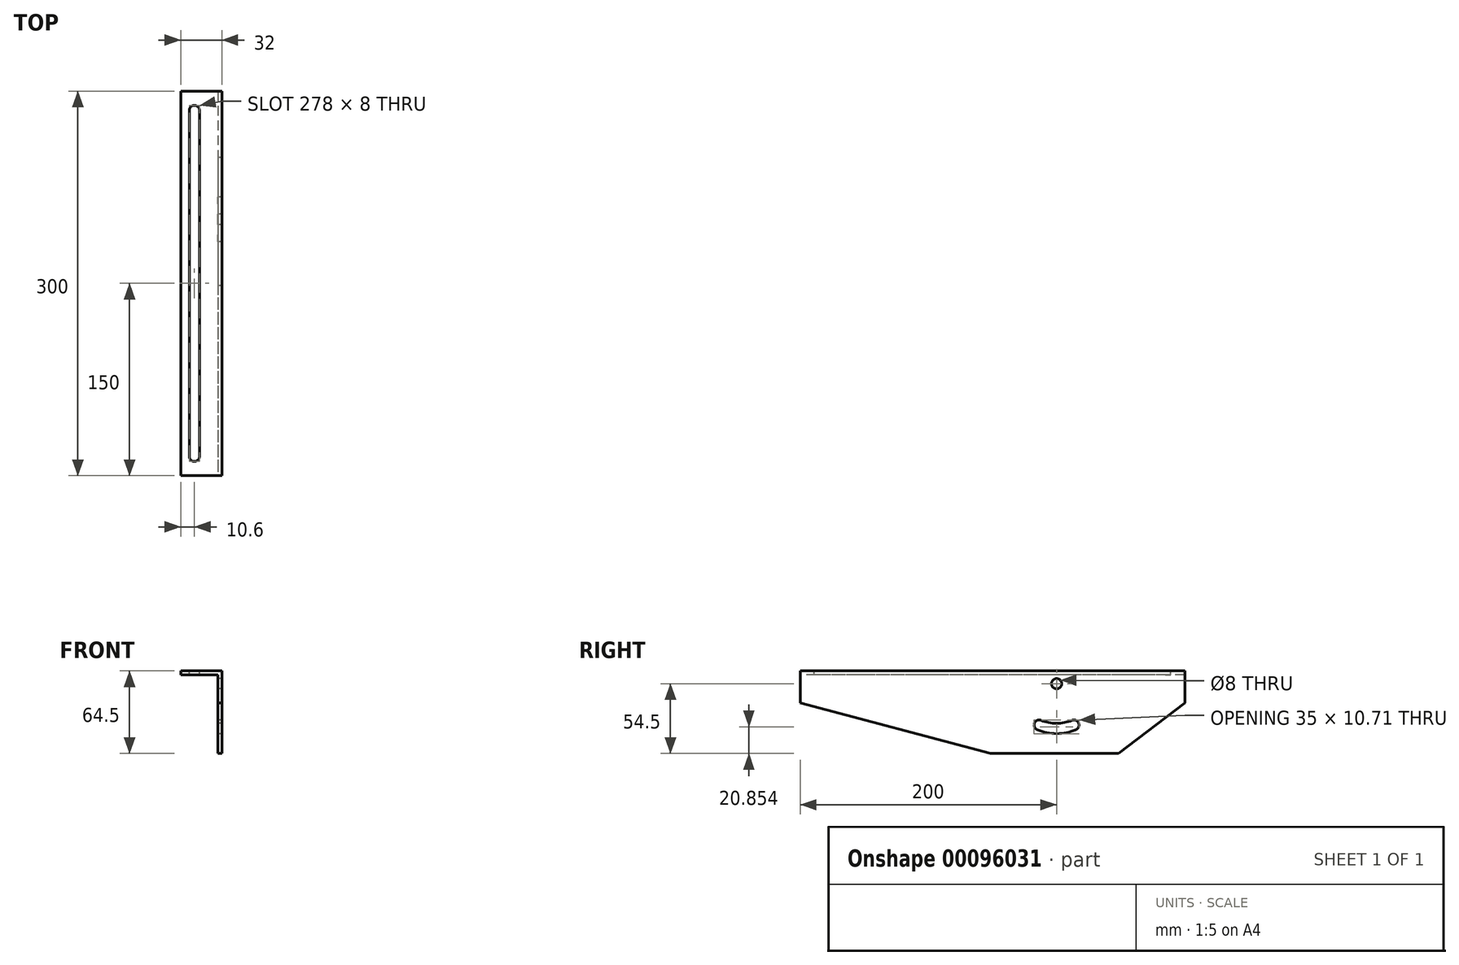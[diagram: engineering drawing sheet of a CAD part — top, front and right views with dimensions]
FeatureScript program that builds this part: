
annotation { "Feature Type Name" : "Feature", "Feature Type Description" : "" }
export const myFeature = defineFeature(function(context is Context, id is Id, definition is map)
    precondition{}
    {
        {
            var Q0;
            Q0=qCreatedBy(makeId("Right.planeOp"),FACE);
            var sketch = newSketch(context, id + "F0", { "sketchPlane" : qUnion([Q0])});
            skLineSegment(sketch, "E0", {"start": v(150, 0) * mm, "end": v(-150, 0) * mm});
            skLineSegment(sketch, "E1", {"start": v(-150, 0) * mm, "end": v(-150, -25) * mm});
            skLineSegment(sketch, "E2", {"start": v(150, 0) * mm, "end": v(150, -25) * mm});
            skLineSegment(sketch, "E3", {"start": v(150, -25) * mm, "end": v(98.38, -64.5) * mm});
            skLineSegment(sketch, "E4", {"start": v(98.38, -64.5) * mm, "end": v(-1.62, -64.5) * mm});
            skLineSegment(sketch, "E5", {"start": v(-1.62, -64.5) * mm, "end": v(-150, -25) * mm});
            skSolve(sketch);
        }
        {
            var Q0;
            Q0=makeQuery(id+"F0.imprint","IMPRINT",FACE,{"disambiguationData":[TD([[makeQuery(id+"F0.imprint","IMPRINT",EDGE,{"derivedFrom":sQuery(id+"F0.wireOp",EDGE,"E0")}),1.0]])]});
            extrude(context, id + "F1", {"entities" : qUnion([Q0]), "depth" : 3 * mm});
        }
        {
            var Q0;
            Q0=makeQuery(id+"F1.opExtrude","CAP_FACE",FACE,{"disambiguationData":[OSD([sQuery(id+"F0.wireOp",EDGE,"E0"),sQuery(id+"F0.wireOp",EDGE,"E1"),sQuery(id+"F0.wireOp",EDGE,"E2"),sQuery(id+"F0.wireOp",EDGE,"E3"),sQuery(id+"F0.wireOp",EDGE,"E4"),sQuery(id+"F0.wireOp",EDGE,"E5")])],"isStart":true});
            var sketch = newSketch(context, id + "F2", { "sketchPlane" : qUnion([Q0])});
            skLineSegment(sketch, "E6.bottom", {"start": v(-150, 0) * mm, "end": v(150, 0) * mm});
            skLineSegment(sketch, "E6.top", {"start": v(-150, -3) * mm, "end": v(150, -3) * mm});
            skLineSegment(sketch, "E6.left", {"start": v(150, 0) * mm, "end": v(150, -3) * mm});
            skLineSegment(sketch, "E6.right", {"start": v(-150, 0) * mm, "end": v(-150, -3) * mm});
            skSolve(sketch);
        }
        {
            var Q0;
            Q0=qSketchRegion(id+"F2",true);
            extrude(context, id + "F3", {"entities" : qUnion([Q0]), "operationType" : NewBodyOperationType.ADD, "depth" : 29 * mm});
        }
        {
            var Q0;
            Q0=makeQuery(id+"F3.boolean.opBoolean","MERGE",FACE,{"derivedFrom":[makeQuery(id+"F1.opExtrude","SWEPT_FACE",FACE,{"disambiguationData":[OSD([sQuery(id+"F0.wireOp",EDGE,"E0")])]}),makeQuery(id+"F3.opExtrude","SWEPT_FACE",FACE,{"disambiguationData":[OSD([sQuery(id+"F2.wireOp",EDGE,"E6.bottom")])]})]});
            var sketch = newSketch(context, id + "F4", { "sketchPlane" : qUnion([Q0])});
            skLineSegment(sketch, "E7", {"start": v(-18.4, 135) * mm, "end": v(-18.4, -135) * mm});
            skArc(sketch, "E8.0.startCap", {"start": v(-14.4, -135) * mm, "mid": v(-18.4, -139) * mm, "end": v(-22.4, -135) * mm});
            skArc(sketch, "E8.0.endCap", {"start": v(-22.4, 135) * mm, "mid": v(-18.4, 139) * mm, "end": v(-14.4, 135) * mm});
            skLineSegment(sketch, "E8.0.left", {"start": v(-22.4, 135) * mm, "end": v(-22.4, -135) * mm});
            skLineSegment(sketch, "E8.0.right", {"start": v(-14.4, 135) * mm, "end": v(-14.4, -135) * mm});
            skSolve(sketch);
        }
        {
            var Q0;
            Q0=qSketchRegion(id+"F4",true);
            extrude(context, id + "F5", {"entities" : qUnion([Q0]), "operationType" : NewBodyOperationType.REMOVE, "endBound" : BoundingType.THROUGH_ALL, "oppositeDirection" : true, "depth" : 25 * mm});
        }
        {
            var Q0;
            Q0=makeQuery(id+"F1.opExtrude","CAP_FACE",FACE,{"disambiguationData":[OSD([sQuery(id+"F0.wireOp",EDGE,"E0"),sQuery(id+"F0.wireOp",EDGE,"E1"),sQuery(id+"F0.wireOp",EDGE,"E2"),sQuery(id+"F0.wireOp",EDGE,"E3"),sQuery(id+"F0.wireOp",EDGE,"E4"),sQuery(id+"F0.wireOp",EDGE,"E5")])],"isStart":true});
            var sketch = newSketch(context, id + "F6", { "sketchPlane" : qUnion([Q0])});
            skCircle(sketch, "E9", {"center": v(-50, -10) * mm, "radius": 4 * mm});
            skArc(sketch, "E10", {"start": v(-63.5, -42.3) * mm, "mid": v(-50, -45) * mm, "end": v(-36.5, -42.3) * mm});
            skArc(sketch, "E11.0.startCap", {"start": v(-65.04, -45.98) * mm, "mid": v(-67.2, -40.75) * mm, "end": v(-61.96, -38.6) * mm});
            skArc(sketch, "E11.0.endCap", {"start": v(-38.04, -38.6) * mm, "mid": v(-32.8, -40.75) * mm, "end": v(-34.96, -45.98) * mm});
            skArc(sketch, "E11.0.left", {"start": v(-61.96, -38.6) * mm, "mid": v(-50, -41) * mm, "end": v(-38.04, -38.6) * mm});
            skArc(sketch, "E11.0.right", {"start": v(-65.04, -45.98) * mm, "mid": v(-50, -49) * mm, "end": v(-34.96, -45.98) * mm});
            skSolve(sketch);
        }
        {
            var Q0;
            Q0=qSketchRegion(id+"F6",true);
            extrude(context, id + "F7", {"entities" : qUnion([Q0]), "operationType" : NewBodyOperationType.REMOVE, "endBound" : BoundingType.THROUGH_ALL, "oppositeDirection" : true, "depth" : 25 * mm});
        }
    });
